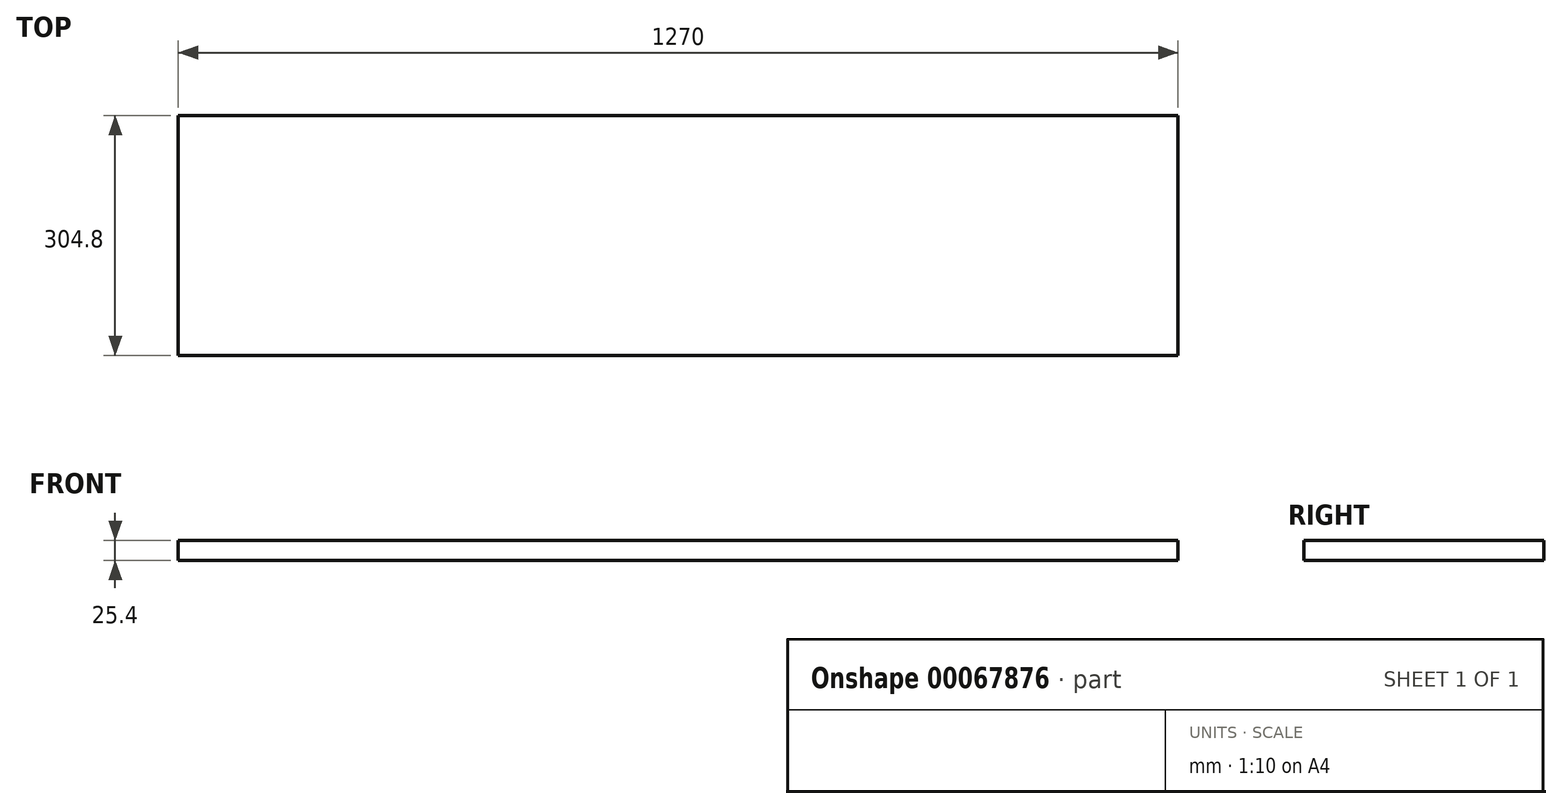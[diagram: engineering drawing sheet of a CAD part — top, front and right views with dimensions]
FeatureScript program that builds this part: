
annotation { "Feature Type Name" : "Feature", "Feature Type Description" : "" }
export const myFeature = defineFeature(function(context is Context, id is Id, definition is map)
    precondition{}
    {
        {
            var Q0;
            Q0=qCreatedBy(makeId("Top.planeOp"),FACE);
            var sketch = newSketch(context, id + "F0", { "sketchPlane" : qUnion([Q0])});
            skLineSegment(sketch, "E0.bottom", {"start": v(0, 0) * mm, "end": v(1270, 0) * mm});
            skLineSegment(sketch, "E0.top", {"start": v(0, 304.8) * mm, "end": v(1270, 304.8) * mm});
            skLineSegment(sketch, "E0.left", {"start": v(0, 0) * mm, "end": v(0, 304.8) * mm});
            skLineSegment(sketch, "E0.right", {"start": v(1270, 0) * mm, "end": v(1270, 304.8) * mm});
            skSolve(sketch);
        }
        {
            var Q0;
            Q0 = qSketchRegion(id + "F0", true);
            extrude(context, id + "F1", {"entities" : qUnion([Q0]), "depth" : 25.4 * mm});
        }
    });
